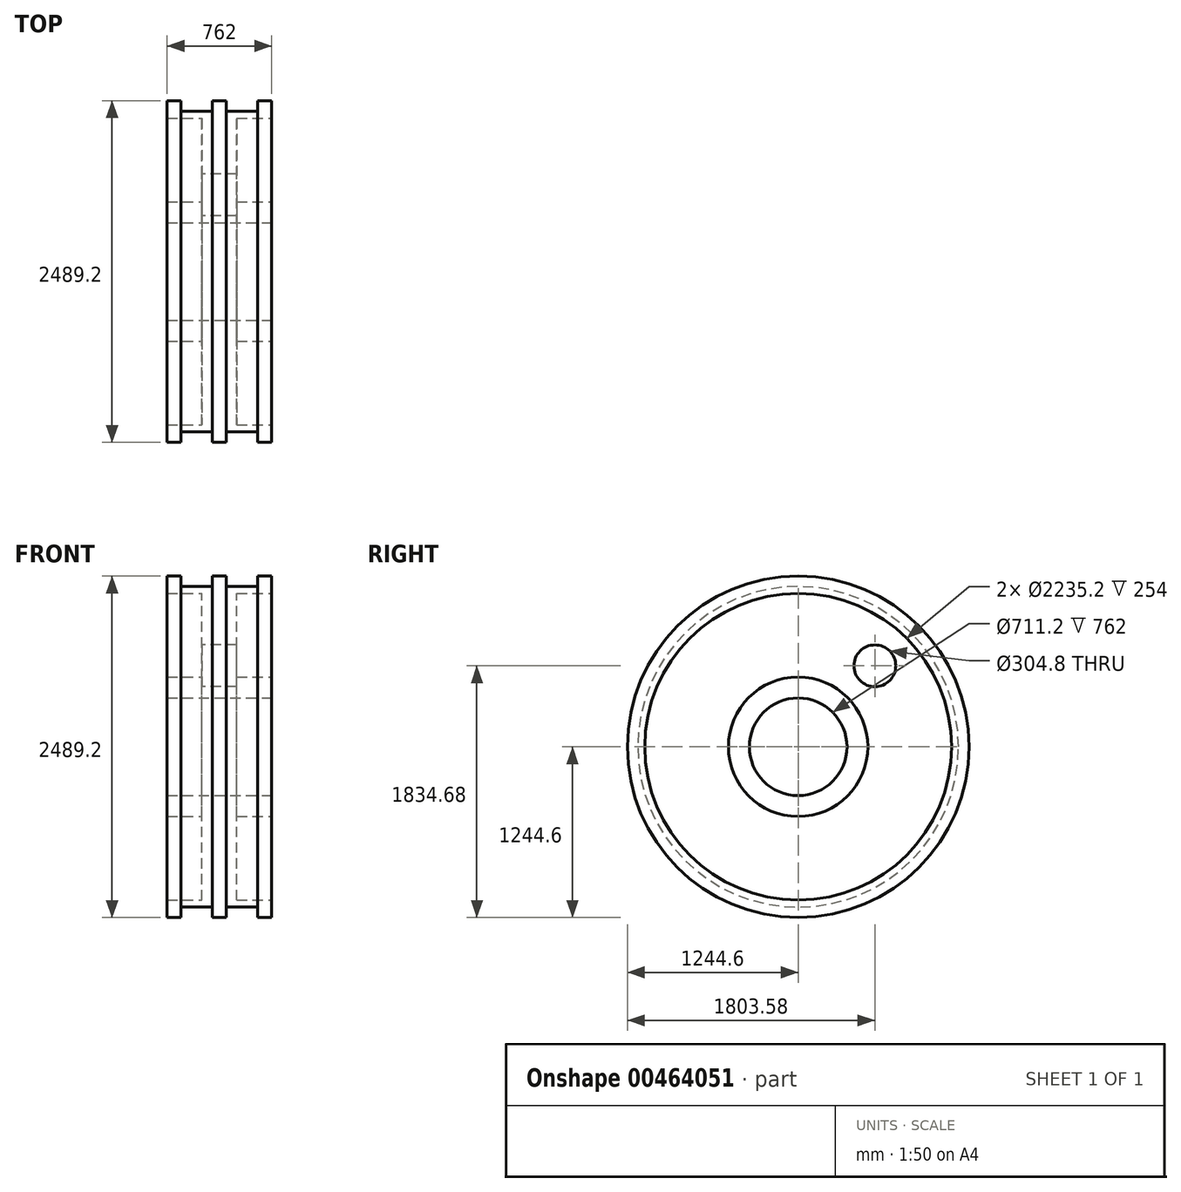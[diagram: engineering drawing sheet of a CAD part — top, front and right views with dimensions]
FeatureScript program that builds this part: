
annotation { "Feature Type Name" : "Feature", "Feature Type Description" : "" }
export const myFeature = defineFeature(function(context is Context, id is Id, definition is map)
    precondition{}
    {
        {
            var Q0;
            Q0=qCreatedBy(makeId("Top.planeOp"),FACE);
            var sketch = newSketch(context, id + "F0", { "sketchPlane" : qUnion([Q0])});
            skLineSegment(sketch, "E0", {"start": v(-381, 812.8) * mm, "end": v(381, 812.8) * mm});
            skLineSegment(sketch, "E1", {"start": v(381, 812.8) * mm, "end": v(381, 660.4) * mm});
            skLineSegment(sketch, "E2", {"start": v(381, 660.4) * mm, "end": v(127, 660.4) * mm});
            skLineSegment(sketch, "E3", {"start": v(127, 660.4) * mm, "end": v(127, 50.8) * mm});
            skLineSegment(sketch, "E4", {"start": v(127, 50.8) * mm, "end": v(381, 50.8) * mm});
            skLineSegment(sketch, "E5", {"start": v(381, 50.8) * mm, "end": v(381, -76.2) * mm});
            skLineSegment(sketch, "E6", {"start": v(381, -76.2) * mm, "end": v(279.4, -76.2) * mm});
            skLineSegment(sketch, "E7", {"start": v(279.4, 0) * mm, "end": v(279.4, -76.2) * mm});
            skLineSegment(sketch, "E8", {"start": v(279.4, 0) * mm, "end": v(50.8, 0) * mm});
            skLineSegment(sketch, "E9", {"start": v(0, 0) * mm, "end": v(0, 1047.37) * mm, "construction": true});
            skLineSegment(sketch, "E10.MirrorCS", {"start": v(-127, 660.4) * mm, "end": v(-127, 50.8) * mm});
            skLineSegment(sketch, "E11.MirrorCS", {"start": v(-381, 812.8) * mm, "end": v(-381, 660.4) * mm});
            skLineSegment(sketch, "E12", {"start": v(50.8, 0) * mm, "end": v(50.8, -76.2) * mm});
            skLineSegment(sketch, "E13", {"start": v(50.8, -76.2) * mm, "end": v(0, -76.2) * mm});
            skLineSegment(sketch, "E14", {"start": v(-381, 660.4) * mm, "end": v(-127, 660.4) * mm});
            skLineSegment(sketch, "E15.MirrorCS", {"start": v(-50.8, -76.2) * mm, "end": v(0, -76.2) * mm});
            skLineSegment(sketch, "E16.MirrorCS", {"start": v(-279.4, 0) * mm, "end": v(-279.4, -76.2) * mm});
            skLineSegment(sketch, "E17.MirrorCS", {"start": v(-381, -76.2) * mm, "end": v(-279.4, -76.2) * mm});
            skLineSegment(sketch, "E18.MirrorCS", {"start": v(-381, 50.8) * mm, "end": v(-381, -76.2) * mm});
            skLineSegment(sketch, "E19.MirrorCS", {"start": v(-127, 50.8) * mm, "end": v(-381, 50.8) * mm});
            skLineSegment(sketch, "E20.MirrorCS", {"start": v(-279.4, 0) * mm, "end": v(-50.8, 0) * mm});
            skLineSegment(sketch, "E21.MirrorCS", {"start": v(-50.8, 0) * mm, "end": v(-50.8, -76.2) * mm});
            skLineSegment(sketch, "E22", {"start": v(0, 812.8) * mm, "end": v(0, 1168.4) * mm, "construction": true});
            skLineSegment(sketch, "E23", {"start": v(0, 1168.4) * mm, "end": v(-76.59, 1168.4) * mm, "construction": true});
            skLineSegment(sketch, "E24.MirrorCS", {"start": v(0, 1168.4) * mm, "end": v(76.59, 1168.4) * mm, "construction": true});
            skSolve(sketch);
        }
        {
            var Q0;
            Q0=makeQuery(id+"F0.imprint","IMPRINT",FACE,{"disambiguationData":[TD([[makeQuery(id+"F0.imprint","IMPRINT",EDGE,{"derivedFrom":sQuery(id+"F0.wireOp",EDGE,"E0")}),-1.0]])]});
            var Q1;
            Q1=sQuery(id+"F0.wireOp",EDGE,"E23");
            revolve(context, id + "F1", {"entities" : qUnion([Q0]), "axis" : qUnion([Q1]), "revolveType" : RevolveType.FULL});
        }
        {
            var Q0;
            Q0=makeQuery(id+"F1.opRevolve","SWEPT_FACE",FACE,{"disambiguationData":[OSD([sQuery(id+"F0.wireOp",EDGE,"E10.MirrorCS")])]});
            var sketch = newSketch(context, id + "F2", { "sketchPlane" : qUnion([Q0])});
            skCircle(sketch, "E25", {"center": v(-1727.37, 590.08) * mm, "radius": 152.4 * mm});
            skSolve(sketch);
        }
        {
            var Q0;
            Q0=makeQuery(id+"F2.imprint","IMPRINT",FACE,{"disambiguationData":[TD([[makeQuery(id+"F2.imprint","IMPRINT",EDGE,{"derivedFrom":sQuery(id+"F2.wireOp",EDGE,"E25")}),1.0]])]});
            extrude(context, id + "F3", {"entities" : qUnion([Q0]), "operationType" : NewBodyOperationType.REMOVE, "oppositeDirection" : true, "depth" : 2230.12 * mm});
        }
        {
            var Q0;
            Q0=makeQuery(id+"F2.imprint","IMPRINT",FACE,{"disambiguationData":[TD([[makeQuery(id+"F2.imprint","IMPRINT",EDGE,{"derivedFrom":sQuery(id+"F2.wireOp",EDGE,"E25")}),1.0]])]});
            var Q1;
            Q1=makeQuery(id+"Fruq7l91YZHjlt5_1.1.F2.imprint","IMPRINT",FACE,{"disambiguationData":[TD([[makeQuery(id+"Fruq7l91YZHjlt5_1.1.F2.imprint","IMPRINT",EDGE,{"derivedFrom":sQuery(id+"Fruq7l91YZHjlt5_1.1.F2.wireOp",EDGE,"E25")}),1.0]])]});
            var Q2;
            Q2=makeQuery(id+"Fruq7l91YZHjlt5_1.2.F2.imprint","IMPRINT",FACE,{"disambiguationData":[TD([[makeQuery(id+"Fruq7l91YZHjlt5_1.2.F2.imprint","IMPRINT",EDGE,{"derivedFrom":sQuery(id+"Fruq7l91YZHjlt5_1.2.F2.wireOp",EDGE,"E25")}),1.0]])]});
            var Q3;
            Q3=makeQuery(id+"Fruq7l91YZHjlt5_1.3.F2.imprint","IMPRINT",FACE,{"disambiguationData":[TD([[makeQuery(id+"Fruq7l91YZHjlt5_1.3.F2.imprint","IMPRINT",EDGE,{"derivedFrom":sQuery(id+"Fruq7l91YZHjlt5_1.3.F2.wireOp",EDGE,"E25")}),1.0]])]});
            var Q4;
            Q4=makeQuery(id+"Fruq7l91YZHjlt5_1.4.F2.imprint","IMPRINT",FACE,{"disambiguationData":[TD([[makeQuery(id+"Fruq7l91YZHjlt5_1.4.F2.imprint","IMPRINT",EDGE,{"derivedFrom":sQuery(id+"Fruq7l91YZHjlt5_1.4.F2.wireOp",EDGE,"E25")}),1.0]])]});
            var Q5;
            Q5=makeQuery(id+"Fruq7l91YZHjlt5_1.5.F2.imprint","IMPRINT",FACE,{"disambiguationData":[TD([[makeQuery(id+"Fruq7l91YZHjlt5_1.5.F2.imprint","IMPRINT",EDGE,{"derivedFrom":sQuery(id+"Fruq7l91YZHjlt5_1.5.F2.wireOp",EDGE,"E25")}),1.0]])]});
            var Q6;
            Q6=makeQuery(id+"Fruq7l91YZHjlt5_1.6.F2.imprint","IMPRINT",FACE,{"disambiguationData":[TD([[makeQuery(id+"Fruq7l91YZHjlt5_1.6.F2.imprint","IMPRINT",EDGE,{"derivedFrom":sQuery(id+"Fruq7l91YZHjlt5_1.6.F2.wireOp",EDGE,"E25")}),1.0]])]});
            extrude(context, id + "F4", {"entities" : qUnion([Q0, Q1, Q2, Q3, Q4, Q5, Q6]), "operationType" : NewBodyOperationType.REMOVE, "endBound" : BoundingType.THROUGH_ALL, "oppositeDirection" : true, "depth" : 25.4 * mm});
        }
    });
